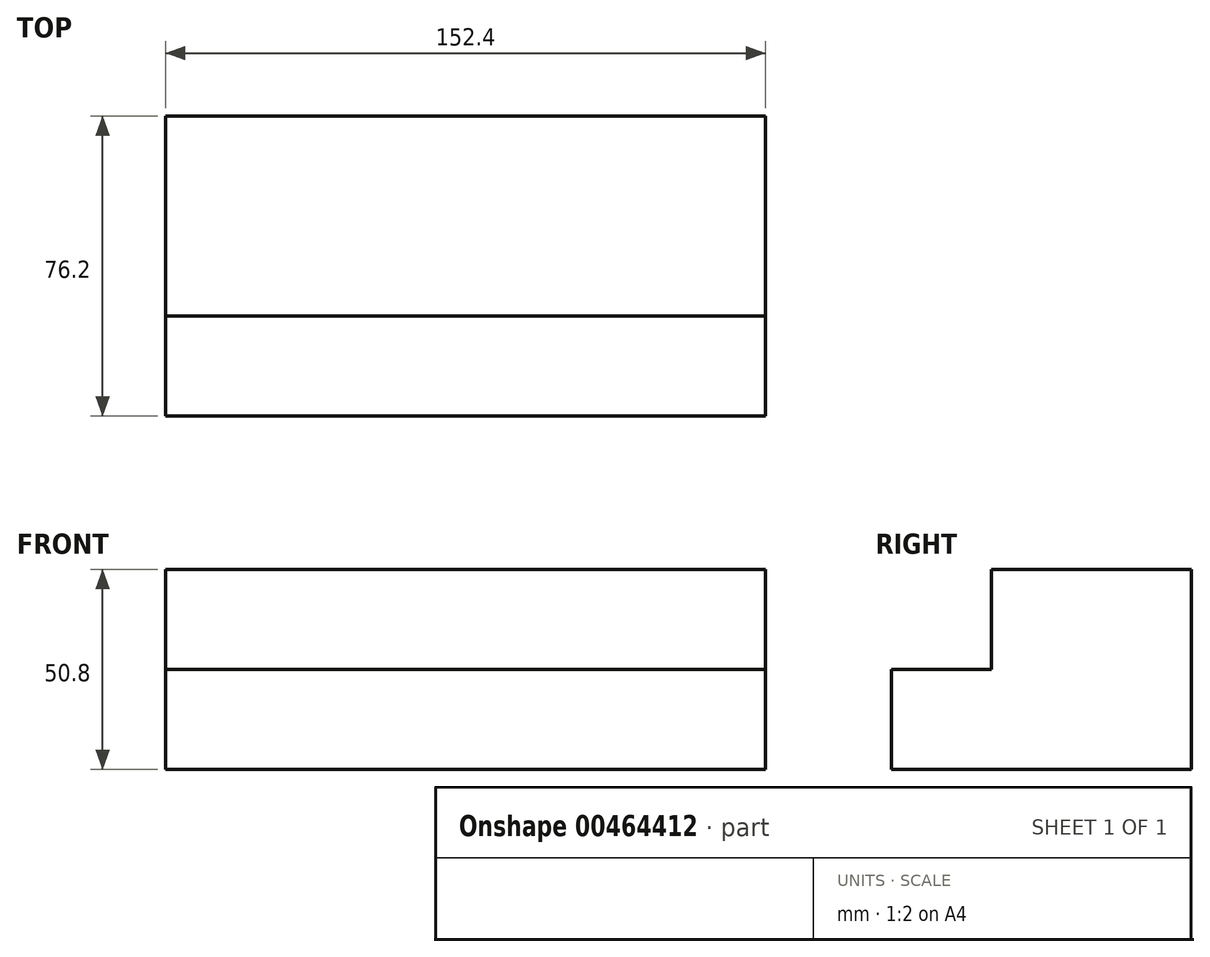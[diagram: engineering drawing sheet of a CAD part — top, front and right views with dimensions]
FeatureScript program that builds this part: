
annotation { "Feature Type Name" : "Feature", "Feature Type Description" : "" }
export const myFeature = defineFeature(function(context is Context, id is Id, definition is map)
    precondition{}
    {
        {
            var Q0;
            Q0=qCreatedBy(makeId("Right.planeOp"),FACE);
            var sketch = newSketch(context, id + "F0", { "sketchPlane" : qUnion([Q0])});
            skLineSegment(sketch, "E0", {"start": v(83.87, 66.94) * mm, "end": v(33.07, 66.94) * mm});
            skLineSegment(sketch, "E1", {"start": v(33.07, 66.94) * mm, "end": v(33.07, 41.54) * mm});
            skLineSegment(sketch, "E2", {"start": v(33.07, 41.54) * mm, "end": v(7.67, 41.54) * mm});
            skLineSegment(sketch, "E3", {"start": v(7.67, 41.54) * mm, "end": v(7.67, 16.14) * mm});
            skLineSegment(sketch, "E4", {"start": v(7.67, 16.14) * mm, "end": v(83.87, 16.14) * mm});
            skLineSegment(sketch, "E5", {"start": v(83.87, 66.94) * mm, "end": v(83.87, 16.14) * mm});
            skSolve(sketch);
        }
        {
            var Q0;
            Q0=makeQuery(id+"F0.imprint","IMPRINT",FACE,{"disambiguationData":[TD([[makeQuery(id+"F0.imprint","IMPRINT",EDGE,{"derivedFrom":sQuery(id+"F0.wireOp",EDGE,"E0")}),1.0]])]});
            extrude(context, id + "F1", {"entities" : qUnion([Q0]), "depth" : 152.4 * mm});
        }
    });
